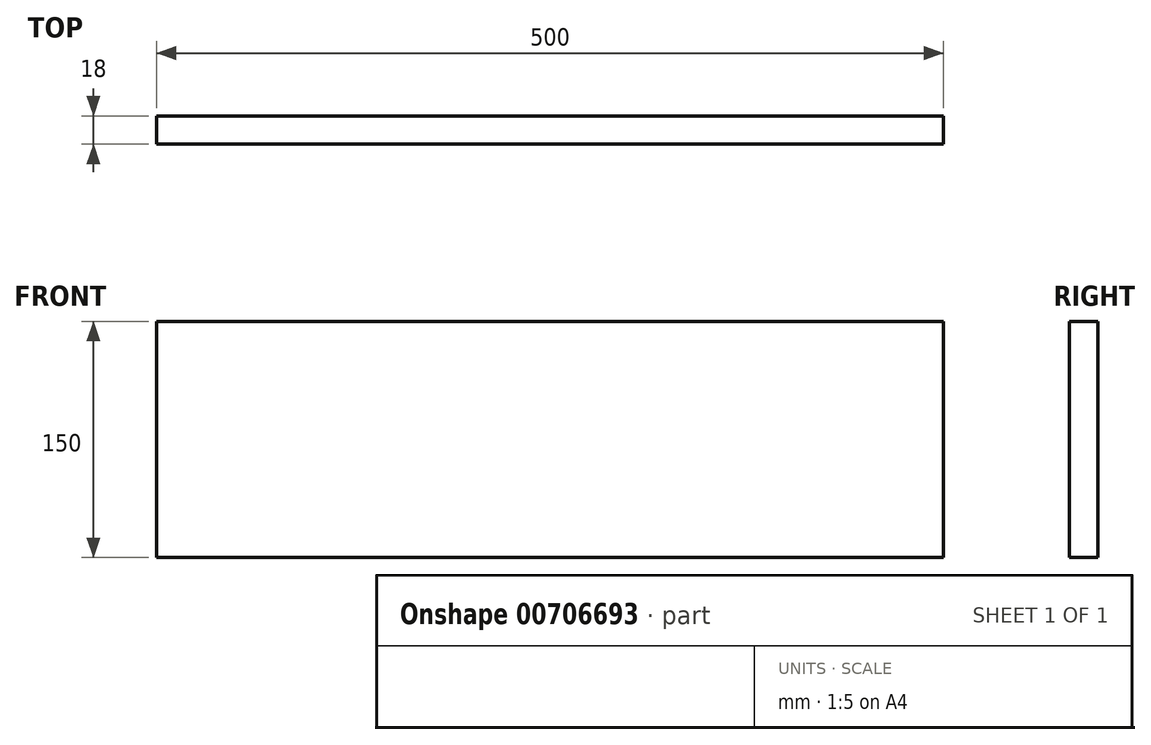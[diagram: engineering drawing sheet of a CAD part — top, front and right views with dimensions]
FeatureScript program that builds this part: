
annotation { "Feature Type Name" : "Feature", "Feature Type Description" : "" }
export const myFeature = defineFeature(function(context is Context, id is Id, definition is map)
    precondition{}
    {
        {
            var Q0;
            Q0=qCreatedBy(makeId("Front.planeOp"),FACE);
            var sketch = newSketch(context, id + "F0", { "sketchPlane" : qUnion([Q0])});
            skLineSegment(sketch, "E0.bottom", {"start": v(-250, -75) * mm, "end": v(250, -75) * mm});
            skLineSegment(sketch, "E0.top", {"start": v(-250, 75) * mm, "end": v(250, 75) * mm});
            skLineSegment(sketch, "E0.left", {"start": v(-250, -75) * mm, "end": v(-250, 75) * mm});
            skLineSegment(sketch, "E0.right", {"start": v(250, -75) * mm, "end": v(250, 75) * mm});
            skPoint(sketch, "E0.middle", {"position": v(0, 0) * mm});
            skSolve(sketch);
        }
        {
            var Q0;
            Q0=makeQuery(id+"F0.imprint","IMPRINT",FACE,{"disambiguationData":[TD([[makeQuery(id+"F0.imprint","IMPRINT",EDGE,{"derivedFrom":sQuery(id+"F0.wireOp",EDGE,"E0.bottom")}),1.0]])]});
            extrude(context, id + "F1", {"entities" : qUnion([Q0]), "depth" : 18 * mm, "offsetDistance" : 25 * mm, "symmetric" : true});
        }
    });
